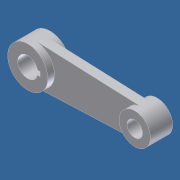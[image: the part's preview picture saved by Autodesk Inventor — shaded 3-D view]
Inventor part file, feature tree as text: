
AUTODESK INVENTOR PART (.ipt)
format: ipt  version: unknown  size: 223,744 bytes
history: native  units: in
note: dims shown in document units (in); Inventor stores cm internally (conversion verified against a paired STEP export)
features: extrude x4, sketch x4, projected_geometry x3, plane x1
ambient origin geometry x8: Origin, YZ Plane, XZ Plane, XY Plane, X Axis, Y Axis, Z Axis, Center Point
bodies: Solid1 (feature_tree)
feature tree (12):
  extrude  "Extrusion1"  Depth=0.875in
  plane  "Work Plane1"
  extrude  "Extrusion2"  Depth=0.563in
  extrude  "Extrusion3"  Depth=0.077in
  extrude  "Extrusion4"  Depth=0.625in TaperAngle=0.0deg
  sketch  "Sketch1"  dims[d0=1.125in d1=0.875in]
  sketch  "Sketch2"  dims[d2=3.0in d3=0.563in]
  projected_geometry  "Projected Loop1"
  projected_geometry  "Projected Loop2"
  sketch  "Sketch3"  dims[d4=0.438in d8=0.077in]
  projected_geometry  "Projected Loop3"
  sketch  "Sketch4"  dims[d9=0.126in d10=0.625in d11=0.0in d12=0.1255in d13=0.0in d14=0.1255in d15=0.0in d16=0.1255in d17=0.0in]
